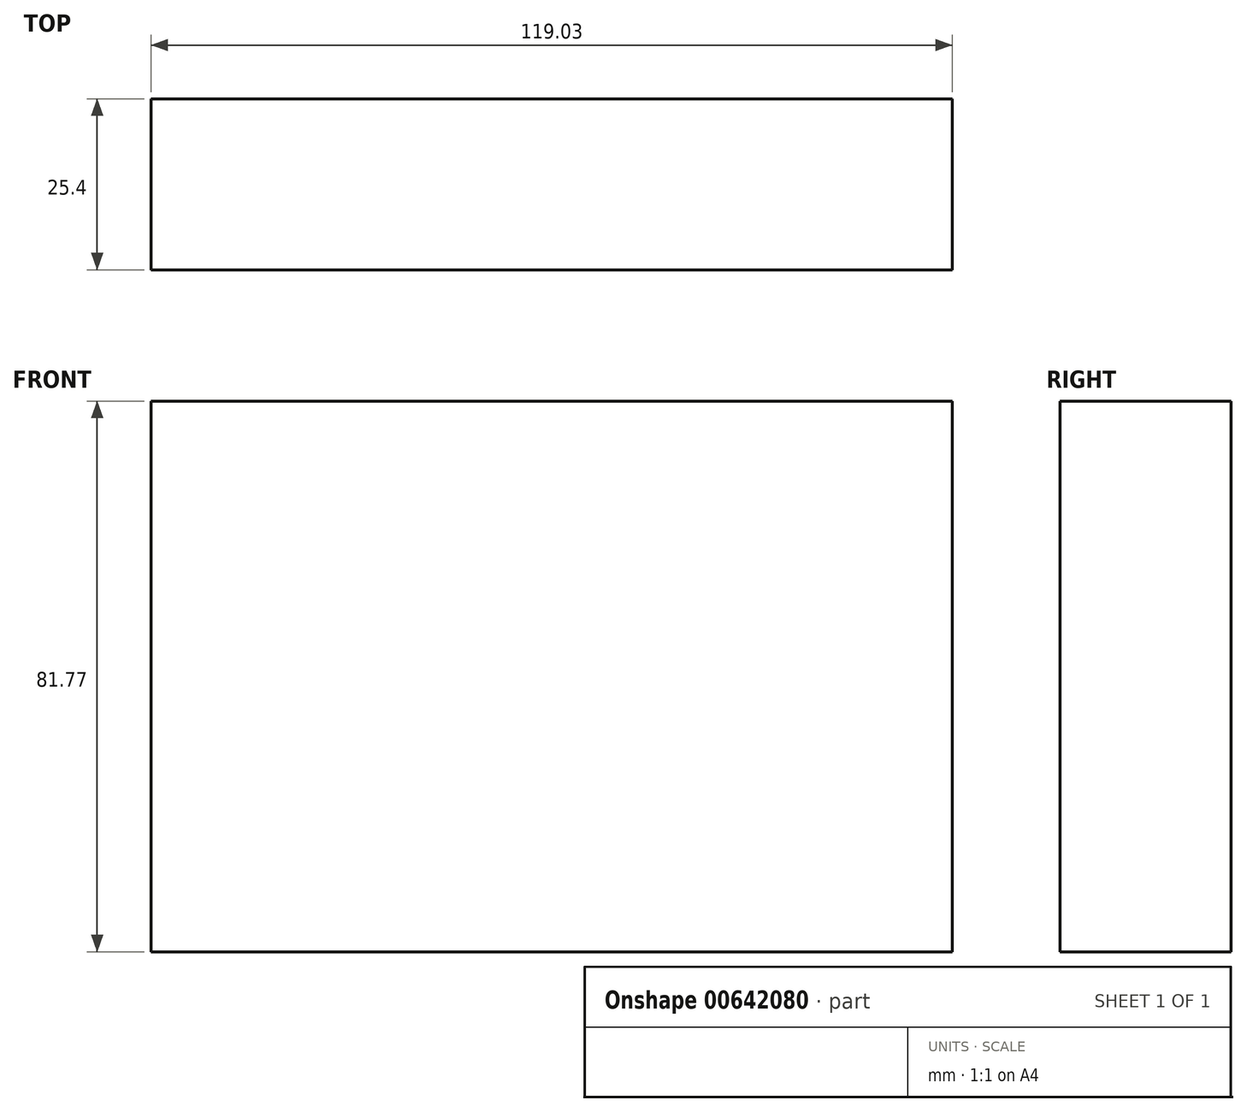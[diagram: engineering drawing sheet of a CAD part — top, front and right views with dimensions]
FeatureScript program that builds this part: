
annotation { "Feature Type Name" : "Feature", "Feature Type Description" : "" }
export const myFeature = defineFeature(function(context is Context, id is Id, definition is map)
    precondition{}
    {
        {
            var Q0;
            Q0=qCreatedBy(makeId("Front.planeOp"),FACE);
            var sketch = newSketch(context, id + "F0", { "sketchPlane" : qUnion([Q0])});
            skLineSegment(sketch, "E0.bottom", {"start": v(-60.2, 39.51) * mm, "end": v(58.83, 39.51) * mm});
            skLineSegment(sketch, "E0.top", {"start": v(-60.2, -42.26) * mm, "end": v(58.83, -42.26) * mm});
            skLineSegment(sketch, "E0.left", {"start": v(-60.2, 39.51) * mm, "end": v(-60.2, -42.26) * mm});
            skLineSegment(sketch, "E0.right", {"start": v(58.83, 39.51) * mm, "end": v(58.83, -42.26) * mm});
            skSolve(sketch);
        }
        {
            var Q0;
            Q0=makeQuery(id+"F0.imprint","IMPRINT",FACE,{"disambiguationData":[TD([[makeQuery(id+"F0.imprint","IMPRINT",EDGE,{"derivedFrom":sQuery(id+"F0.wireOp",EDGE,"E0.bottom")}),-1.0]])]});
            extrude(context, id + "F1", {"entities" : qUnion([Q0]), "depth" : 25.4 * mm, "offsetDistance" : 25.4 * mm});
        }
    });
